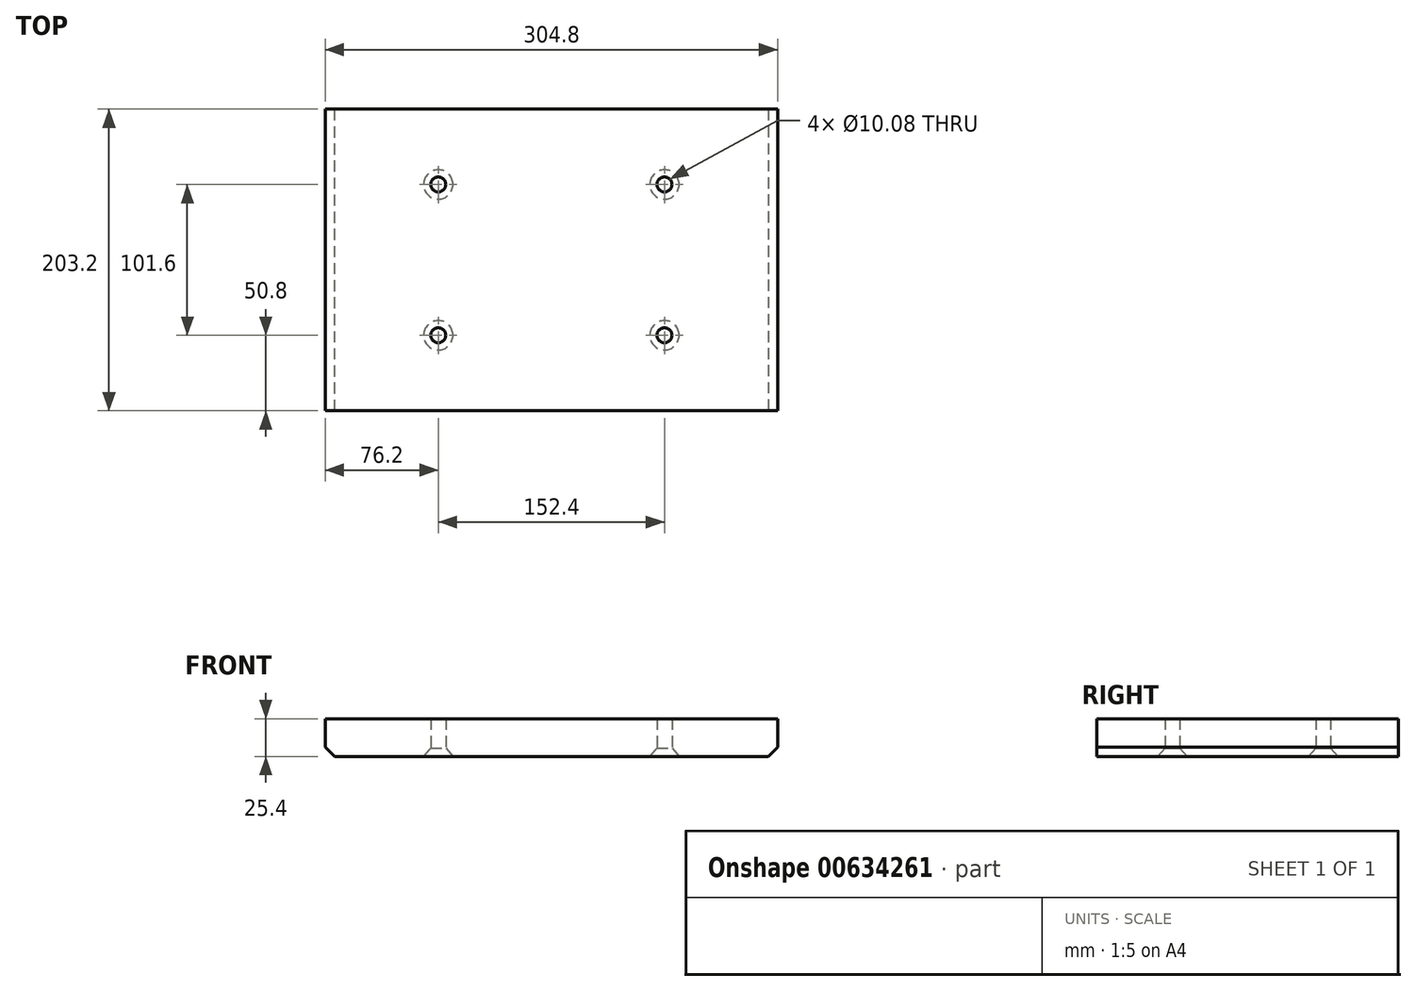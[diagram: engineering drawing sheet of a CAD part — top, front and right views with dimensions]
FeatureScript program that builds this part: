
annotation { "Feature Type Name" : "Feature", "Feature Type Description" : "" }
export const myFeature = defineFeature(function(context is Context, id is Id, definition is map)
    precondition{}
    {
        {
            var Q0;
            Q0=qCreatedBy(makeId("Front.planeOp"),FACE);
            var sketch = newSketch(context, id + "F0", { "sketchPlane" : qUnion([Q0])});
            skLineSegment(sketch, "E0.bottom", {"start": v(152.4, -12.7) * mm, "end": v(-152.4, -12.7) * mm});
            skLineSegment(sketch, "E0.top", {"start": v(152.4, 12.7) * mm, "end": v(-152.4, 12.7) * mm});
            skLineSegment(sketch, "E0.left", {"start": v(152.4, -12.7) * mm, "end": v(152.4, 12.7) * mm});
            skLineSegment(sketch, "E0.right", {"start": v(-152.4, -12.7) * mm, "end": v(-152.4, 12.7) * mm});
            skPoint(sketch, "E0.middle", {"position": v(0, 0) * mm});
            skSolve(sketch);
        }
        {
            var Q0;
            Q0 = qSketchRegion(id + "F0", true);
            extrude(context, id + "F1", {"entities" : qUnion([Q0]), "endBound" : BoundingType.SYMMETRIC, "depth" : 203.2 * mm, "offsetDistance" : 25.4 * mm});
        }
        {
            var Q0;
            Q0=makeQuery(id+"F1.opExtrude","SWEPT_EDGE",EDGE,{"disambiguationData":[OSD([sQuery(id+"F0.wireOp",EDGE,"E0.bottom"),sQuery(id+"F0.wireOp",EDGE,"E0.left")])]});
            var Q1;
            Q1=makeQuery(id+"F1.opExtrude","SWEPT_EDGE",EDGE,{"disambiguationData":[OSD([sQuery(id+"F0.wireOp",EDGE,"E0.bottom"),sQuery(id+"F0.wireOp",EDGE,"E0.right")])]});
            chamfer(context, id + "F2", {"entities" : qUnion([Q0, Q1]), "width" : 6.35 * mm, "tangentPropagation" : true});
        }
        {
            var Q0;
            Q0=makeQuery(id+"F1.opExtrude","SWEPT_FACE",FACE,{"disambiguationData":[OSD([sQuery(id+"F0.wireOp",EDGE,"E0.bottom")])]});
            var sketch = newSketch(context, id + "F3", { "sketchPlane" : qUnion([Q0])});
            skLineSegment(sketch, "E1", {"start": v(-151.53, 50.8) * mm, "end": v(168.98, 50.8) * mm, "construction": true});
            skLineSegment(sketch, "E2", {"start": v(-76.2, 121.77) * mm, "end": v(-76.2, -129.62) * mm, "construction": true});
            skLineSegment(sketch, "E3.MirrorCS", {"start": v(76.2, 121.77) * mm, "end": v(76.2, -129.62) * mm, "construction": true});
            skLineSegment(sketch, "E4.MirrorCS", {"start": v(-151.53, -50.8) * mm, "end": v(168.98, -50.8) * mm, "construction": true});
            skPoint(sketch, "E5", {"position": v(-76.2, 50.8) * mm});
            skPoint(sketch, "E6", {"position": v(76.2, 50.8) * mm});
            skPoint(sketch, "E7", {"position": v(76.2, -50.8) * mm});
            skPoint(sketch, "E8", {"position": v(-76.2, -50.8) * mm});
            skSolve(sketch);
        }
        {
            var Q0;
            Q0=sQuery(id+"F3.wireOp",VERTEX,"E5");
            var Q1;
            Q1=sQuery(id+"F3.wireOp",VERTEX,"E6");
            var Q2;
            Q2=sQuery(id+"F3.wireOp",VERTEX,"E7");
            var Q3;
            Q3=sQuery(id+"F3.wireOp",VERTEX,"E8");
            var Q4;
            Q4=makeQuery(id+"F1.opExtrude","SWEPT_BODY",BODY,{"disambiguationData":[OSD([sQuery(id+"F0.wireOp",EDGE,"E0.bottom"),sQuery(id+"F0.wireOp",EDGE,"E0.top"),sQuery(id+"F0.wireOp",EDGE,"E0.left"),sQuery(id+"F0.wireOp",EDGE,"E0.right")])]});
            hole(context, id + "F4", {"style" : HoleStyle.C_SINK, "endStyle" : HoleEndStyle.THROUGH, "standardTappedOrClearance" : lookupTablePath({ "standard" : "ANSI", "fit" : "Normal (ASME)", "size" : "3/8", "type" : "Clearance" }), "standardBlindInLast" : lookupTablePath({ "fit" : "Free", "standard" : "ANSI", "size" : "3/8", "type" : "Clearance" }), "holeDiameter" : 10.08 * mm, "cSinkDiameter" : 19.84 * mm, "cSinkAngle" : 82 * degree, "majorDiameter" : 6.35 * mm, "isTappedThrough" : true, "tappedDepth" : 12.7 * mm, "tapClearance" : 3, "locations" : qUnion([Q0, Q1, Q2, Q3]), "scope" : qUnion([Q4])});
        }
    });
